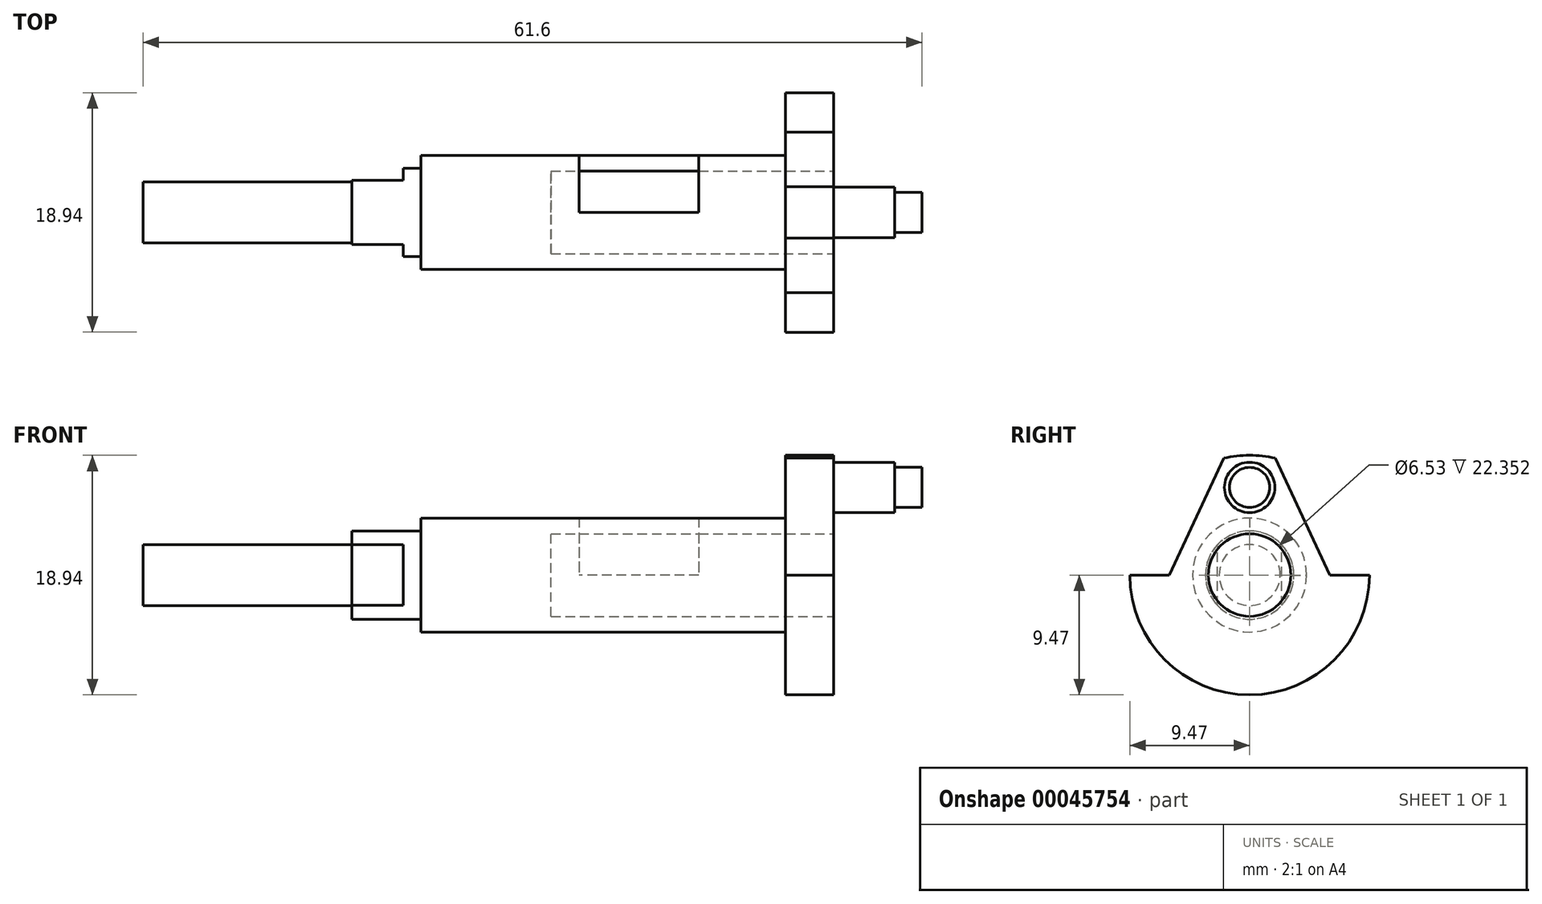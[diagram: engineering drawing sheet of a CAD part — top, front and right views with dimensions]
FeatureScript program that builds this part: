
annotation { "Feature Type Name" : "Feature", "Feature Type Description" : "" }
export const myFeature = defineFeature(function(context is Context, id is Id, definition is map)
    precondition{}
    {
        {
            var Q0;
            Q0=qCreatedBy(makeId("Front.planeOp"),FACE);
            var sketch = newSketch(context, id + "F0", { "sketchPlane" : qUnion([Q0])});
            skLineSegment(sketch, "E0", {"start": v(-27.3, 0) * mm, "end": v(27.3, 0) * mm});
            skLineSegment(sketch, "E1", {"start": v(-27.3, 0) * mm, "end": v(-27.3, 2.41) * mm});
            skLineSegment(sketch, "E2", {"start": v(-27.3, 2.41) * mm, "end": v(-10.8, 2.41) * mm});
            skLineSegment(sketch, "E3", {"start": v(-10.8, 2.41) * mm, "end": v(-10.8, 3.5) * mm});
            skLineSegment(sketch, "E4", {"start": v(-10.8, 3.5) * mm, "end": v(-5.33, 3.5) * mm});
            skLineSegment(sketch, "E5", {"start": v(-5.33, 3.5) * mm, "end": v(-5.33, 4.5) * mm});
            skLineSegment(sketch, "E6", {"start": v(-5.33, 4.5) * mm, "end": v(23.5, 4.5) * mm});
            skLineSegment(sketch, "E7", {"start": v(23.5, 9.47) * mm, "end": v(27.3, 9.47) * mm});
            skLineSegment(sketch, "E8", {"start": v(27.3, 9.47) * mm, "end": v(27.3, 0) * mm});
            skLineSegment(sketch, "E9", {"start": v(23.5, 4.5) * mm, "end": v(23.5, 9.47) * mm});
            skSolve(sketch);
        }
        {
            var Q0;
            Q0=makeQuery(id+"F0.imprint","IMPRINT",FACE,{"disambiguationData":[TD([[makeQuery(id+"F0.imprint","IMPRINT",EDGE,{"derivedFrom":sQuery(id+"F0.wireOp",EDGE,"E0")}),1.0]])]});
            var Q1;
            Q1=sQuery(id+"F0.wireOp",EDGE,"E0");
            revolve(context, id + "F1", {"entities" : qUnion([Q0]), "axis" : qUnion([Q1]), "revolveType" : RevolveType.FULL});
        }
        {
            var Q0;
            Q0=makeQuery(id+"F1.opRevolve","SWEPT_FACE",FACE,{"disambiguationData":[OSD([sQuery(id+"F0.wireOp",EDGE,"E8")])]});
            var sketch = newSketch(context, id + "F2", { "sketchPlane" : qUnion([Q0])});
            skLineSegment(sketch, "E10", {"start": v(-9.47, 0) * mm, "end": v(-6.35, 0) * mm});
            skLineSegment(sketch, "E11", {"start": v(-6.35, 0) * mm, "end": v(-2.04, 9.25) * mm});
            skLineSegment(sketch, "E12", {"start": v(0, 0) * mm, "end": v(0, 9.47) * mm, "construction": true});
            skLineSegment(sketch, "E13.MirrorCS", {"start": v(9.47, 0) * mm, "end": v(6.35, 0) * mm});
            skLineSegment(sketch, "E14.MirrorCS", {"start": v(6.35, 0) * mm, "end": v(2.04, 9.25) * mm});
            skArc(sketch, "E15", {"start": v(-2.04, 9.25) * mm, "mid": v(-7.38, 5.94) * mm, "end": v(-9.47, 0) * mm});
            skArc(sketch, "E16.trimOffspring", {"start": v(9.47, 0) * mm, "mid": v(7.38, 5.94) * mm, "end": v(2.04, 9.25) * mm});
            skSolve(sketch);
        }
        {
            var Q0;
            Q0 = qSketchRegion(id + "F2", true);
            var Q1;
            Q1=makeQuery(id+"F1.opRevolve","SWEPT_FACE",FACE,{"disambiguationData":[OSD([sQuery(id+"F0.wireOp",EDGE,"E9")])]});
            extrude(context, id + "F3", {"entities" : qUnion([Q0]), "operationType" : NewBodyOperationType.REMOVE, "endBound" : BoundingType.UP_TO_SURFACE, "oppositeDirection" : true, "endBoundEntityFace" : qUnion([Q1]), "depth" : 25.4 * mm});
        }
        {
            var Q0;
            Q0=makeQuery(id+"F1.opRevolve","SWEPT_FACE",FACE,{"disambiguationData":[OSD([sQuery(id+"F0.wireOp",EDGE,"E8")])]});
            var sketch = newSketch(context, id + "F4", { "sketchPlane" : qUnion([Q0])});
            skCircle(sketch, "E17", {"center": v(0, 0) * mm, "radius": 3.26 * mm});
            skSolve(sketch);
        }
        {
            var Q0;
            Q0 = qSketchRegion(id + "F4", true);
            extrude(context, id + "F5", {"entities" : qUnion([Q0]), "operationType" : NewBodyOperationType.REMOVE, "oppositeDirection" : true, "depth" : 22.35 * mm});
        }
        {
            var Q0;
            Q0=makeQuery(id+"F1.opRevolve","SWEPT_FACE",FACE,{"disambiguationData":[OSD([sQuery(id+"F0.wireOp",EDGE,"E8")])]});
            var sketch = newSketch(context, id + "F6", { "sketchPlane" : qUnion([Q0])});
            skCircle(sketch, "E18", {"center": v(0, 6.93) * mm, "radius": 2 * mm});
            skSolve(sketch);
        }
        {
            var Q0;
            Q0=makeQuery(id+"F6.imprint","IMPRINT",FACE,{"disambiguationData":[TD([[makeQuery(id+"F6.imprint","IMPRINT",EDGE,{"derivedFrom":sQuery(id+"F6.wireOp",EDGE,"E18")}),1.0]])]});
            extrude(context, id + "F7", {"entities" : qUnion([Q0]), "operationType" : NewBodyOperationType.ADD, "depth" : 4.83 * mm});
        }
        {
            var Q0;
            Q0=makeQuery(id+"F7.opExtrude","CAP_FACE",FACE,{"disambiguationData":[OSD([sQuery(id+"F6.wireOp",EDGE,"E18")])],"isStart":false});
            var sketch = newSketch(context, id + "F8", { "sketchPlane" : qUnion([Q0])});
            skCircle(sketch, "E19", {"center": v(0, 6.93) * mm, "radius": 1.59 * mm});
            skSolve(sketch);
        }
        {
            var Q0;
            Q0 = qSketchRegion(id + "F8", true);
            extrude(context, id + "F9", {"entities" : qUnion([Q0]), "operationType" : NewBodyOperationType.ADD, "depth" : 2.16 * mm});
        }
        {
            var Q0;
            Q0=qCreatedBy(makeId("Top.planeOp"),FACE);
            var sketch = newSketch(context, id + "F10", { "sketchPlane" : qUnion([Q0])});
            skLineSegment(sketch, "E20.rect.bottom", {"start": v(16.64, 0) * mm, "end": v(7.19, 0) * mm});
            skLineSegment(sketch, "E20.rect.top", {"start": v(16.64, 4.5) * mm, "end": v(7.19, 4.5) * mm});
            skLineSegment(sketch, "E20.rect.left", {"start": v(16.64, 0) * mm, "end": v(16.64, 4.5) * mm});
            skLineSegment(sketch, "E20.rect.right", {"start": v(7.19, 0) * mm, "end": v(7.19, 4.5) * mm});
            skPoint(sketch, "E20.rect.middle", {"position": v(11.91, 2.25) * mm});
            skSolve(sketch);
        }
        {
            var Q0;
            Q0 = qSketchRegion(id + "F10", true);
            extrude(context, id + "F11", {"entities" : qUnion([Q0]), "operationType" : NewBodyOperationType.REMOVE, "depth" : 25.4 * mm});
        }
        {
            var Q0;
            Q0=qCreatedBy(makeId("Top.planeOp"),FACE);
            var sketch = newSketch(context, id + "F12", { "sketchPlane" : qUnion([Q0])});
            skLineSegment(sketch, "E21.rect.bottom", {"start": v(-6.73, -6.35) * mm, "end": v(-10.8, -6.35) * mm});
            skLineSegment(sketch, "E21.rect.top", {"start": v(-6.73, -2.54) * mm, "end": v(-10.8, -2.54) * mm});
            skLineSegment(sketch, "E21.rect.left", {"start": v(-6.73, -6.35) * mm, "end": v(-6.73, -2.54) * mm});
            skLineSegment(sketch, "E21.rect.right", {"start": v(-10.8, -6.35) * mm, "end": v(-10.8, -2.54) * mm});
            skPoint(sketch, "E21.rect.middle", {"position": v(-8.76, -4.45) * mm});
            skLineSegment(sketch, "E22", {"start": v(-27.33, 0) * mm, "end": v(34.2, 0) * mm, "construction": true});
            skLineSegment(sketch, "E23.MirrorCS", {"start": v(-6.73, 6.35) * mm, "end": v(-10.8, 6.35) * mm});
            skLineSegment(sketch, "E24.MirrorCS", {"start": v(-6.73, 2.54) * mm, "end": v(-10.8, 2.54) * mm});
            skLineSegment(sketch, "E25.MirrorCS", {"start": v(-6.73, 6.35) * mm, "end": v(-6.73, 2.54) * mm});
            skLineSegment(sketch, "E26.MirrorCS", {"start": v(-10.8, 6.35) * mm, "end": v(-10.8, 2.54) * mm});
            skPoint(sketch, "E27.MirrorP", {"position": v(-8.76, 4.45) * mm});
            skSolve(sketch);
        }
        {
            var Q0;
            Q0 = qSketchRegion(id + "F12", true);
            extrude(context, id + "F13", {"entities" : qUnion([Q0]), "operationType" : NewBodyOperationType.REMOVE, "endBound" : BoundingType.THROUGH_ALL, "oppositeDirection" : true, "depth" : 25.4 * mm, "hasSecondDirection" : true, "secondDirectionBound" : SecondDirectionBoundingType.THROUGH_ALL, "secondDirectionOppositeDirection" : false, "secondDirectionDepth" : 25.4 * mm});
        }
    });
